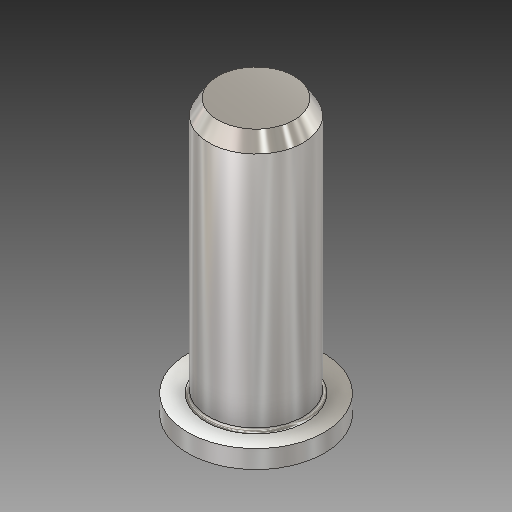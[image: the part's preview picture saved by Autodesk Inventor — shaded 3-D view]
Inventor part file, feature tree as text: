
AUTODESK INVENTOR PART (.ipt)
format: ipt  version: 2019 (Build 230136000, 136)  size: 161,280 bytes
history: native  units: in
note: dims shown in document units (in); Inventor stores cm internally (conversion verified against a paired STEP export)
features: other x3, sketch x2
ambient origin geometry x8: Origin, YZ Plane, XZ Plane, XY Plane, X Axis, Y Axis, Z Axis, Center Point
bodies: Solid1 (feature_tree)
feature tree (5):
  other  "Pivot Pin A.ipt"
  other  "Solid1::Pivot Pin A.ipt"
  other  "TaggingFeature1"
  sketch  "Sketch1"  dims[d0=0.3937in]
  sketch  "Sketch2"
